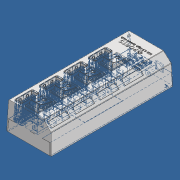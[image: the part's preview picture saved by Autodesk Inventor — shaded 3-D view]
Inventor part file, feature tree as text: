
AUTODESK INVENTOR PART (.ipt)
format: ipt  version: 2021 (Build 250183000, 183)  size: 6,049,792 bytes
history: native  units: mm
features: other x54, extrude x1, sketch x1
ambient origin geometry x8: Origin, YZ Plane, XZ Plane, XY Plane, X Axis, Y Axis, Z Axis, Center Point
bodies: Solid1 (feature_tree), Solid39 (feature_tree), Solid40 (feature_tree), Solid41 (feature_tree), Solid42 (feature_tree), Solid43 (feature_tree), Solid44 (feature_tree), Solid45 (feature_tree), Solid46 (feature_tree), Solid47 (feature_tree), Solid48 (feature_tree), Solid49 (feature_tree), Solid50 (feature_tree), Solid51 (feature_tree), Solid52 (feature_tree), Solid53 (feature_tree), Solid54 (feature_tree), Solid55 (feature_tree), Solid56 (feature_tree), Solid57 (feature_tree), Solid58 (feature_tree), Solid59 (feature_tree), Solid60 (feature_tree), Solid61 (feature_tree), Solid62 (feature_tree), Solid63 (feature_tree), Solid64 (feature_tree), Solid65 (feature_tree), Solid66 (feature_tree), Solid67 (feature_tree), Solid68 (feature_tree), Solid69 (feature_tree), Solid70 (feature_tree), Solid71 (feature_tree), Solid72 (feature_tree), Solid73 (feature_tree), Solid74 (feature_tree), Solid75 (feature_tree), Solid76 (feature_tree), Solid77 (feature_tree), Solid78 (feature_tree), Solid79 (feature_tree), Solid80 (feature_tree), Solid81 (feature_tree), Solid82 (feature_tree), Solid83 (feature_tree), Solid84 (feature_tree), Solid85 (feature_tree), Solid86 (feature_tree), Solid89 (feature_tree), Solid90 (feature_tree), Solid91 (feature_tree), Solid92 (feature_tree), Solid93 (feature_tree)
feature tree (56):
  extrude  "Extrusion1"  [1 undecoded]
  sketch  "Sketch2"  dims[d0=65.0mm d1=0.0mm]
  other  "HUB 7 port-1-solid1"
  other  "USB 3.0 A -Female port_vertical -4-solid1"
  other  "USB 3.0 A -Female port_vertical -4-solid2"
  other  "USB 3.0 A -Female port_vertical -4-solid3"
  other  "USB 3.0 A -Female port_vertical -4-solid4"
  other  "USB 3.0 A -Female port_vertical -4-solid5"
  other  "USB 3.0 A -Female port_vertical -4-solid6"
  other  "USB 3.0 A -Female port_vertical -4-solid7"
  other  "USB 3.0 A -Female port_vertical -4-solid8"
  other  "USB 3.0 A -Female port_vertical -4-solid9"
  other  "USB 3.0 A -Female port_vertical -4-solid10"
  other  "USB 3.0 A -Female port_vertical -4-solid11"
  other  "USB 3.0 A -Female port_vertical -4-solid12"
  other  "USB 3.0 A -Female port_vertical -5-solid1"
  other  "USB 3.0 A -Female port_vertical -5-solid2"
  other  "USB 3.0 A -Female port_vertical -5-solid3"
  other  "USB 3.0 A -Female port_vertical -5-solid4"
  other  "USB 3.0 A -Female port_vertical -5-solid5"
  other  "USB 3.0 A -Female port_vertical -5-solid6"
  other  "USB 3.0 A -Female port_vertical -5-solid7"
  other  "USB 3.0 A -Female port_vertical -5-solid8"
  other  "USB 3.0 A -Female port_vertical -5-solid9"
  other  "USB 3.0 A -Female port_vertical -5-solid10"
  other  "USB 3.0 A -Female port_vertical -5-solid11"
  other  "USB 3.0 A -Female port_vertical -5-solid12"
  other  "USB 3.0 A -Female port_vertical -6-solid1"
  other  "USB 3.0 A -Female port_vertical -6-solid2"
  other  "USB 3.0 A -Female port_vertical -6-solid3"
  other  "USB 3.0 A -Female port_vertical -6-solid4"
  other  "USB 3.0 A -Female port_vertical -6-solid5"
  other  "USB 3.0 A -Female port_vertical -6-solid6"
  other  "USB 3.0 A -Female port_vertical -6-solid7"
  other  "USB 3.0 A -Female port_vertical -6-solid8"
  other  "USB 3.0 A -Female port_vertical -6-solid9"
  other  "USB 3.0 A -Female port_vertical -6-solid10"
  other  "USB 3.0 A -Female port_vertical -6-solid11"
  other  "USB 3.0 A -Female port_vertical -6-solid12"
  other  "USB 3.0 A -Female port_vertical -7-solid1"
  other  "USB 3.0 A -Female port_vertical -7-solid2"
  other  "USB 3.0 A -Female port_vertical -7-solid3"
  other  "USB 3.0 A -Female port_vertical -7-solid4"
  other  "USB 3.0 A -Female port_vertical -7-solid5"
  other  "USB 3.0 A -Female port_vertical -7-solid6"
  other  "USB 3.0 A -Female port_vertical -7-solid7"
  other  "USB 3.0 A -Female port_vertical -7-solid8"
  other  "USB 3.0 A -Female port_vertical -7-solid9"
  other  "USB 3.0 A -Female port_vertical -7-solid10"
  other  "USB 3.0 A -Female port_vertical -7-solid11"
  other  "USB 3.0 A -Female port_vertical -7-solid12"
  other  "switch_full-4-solid1"
  other  "switch_full-5-solid1"
  other  "switch_full-6-solid1"
  other  "switch_full-7-solid1"
  other  "USB-3-0-Type-Micro-B-plug-1-solid1"
note: 1 required parameter value undecoded (feature->parameter linkage not recoverable at this tier; creation-order binding heuristic only, values carry confidence <= 0.55)
